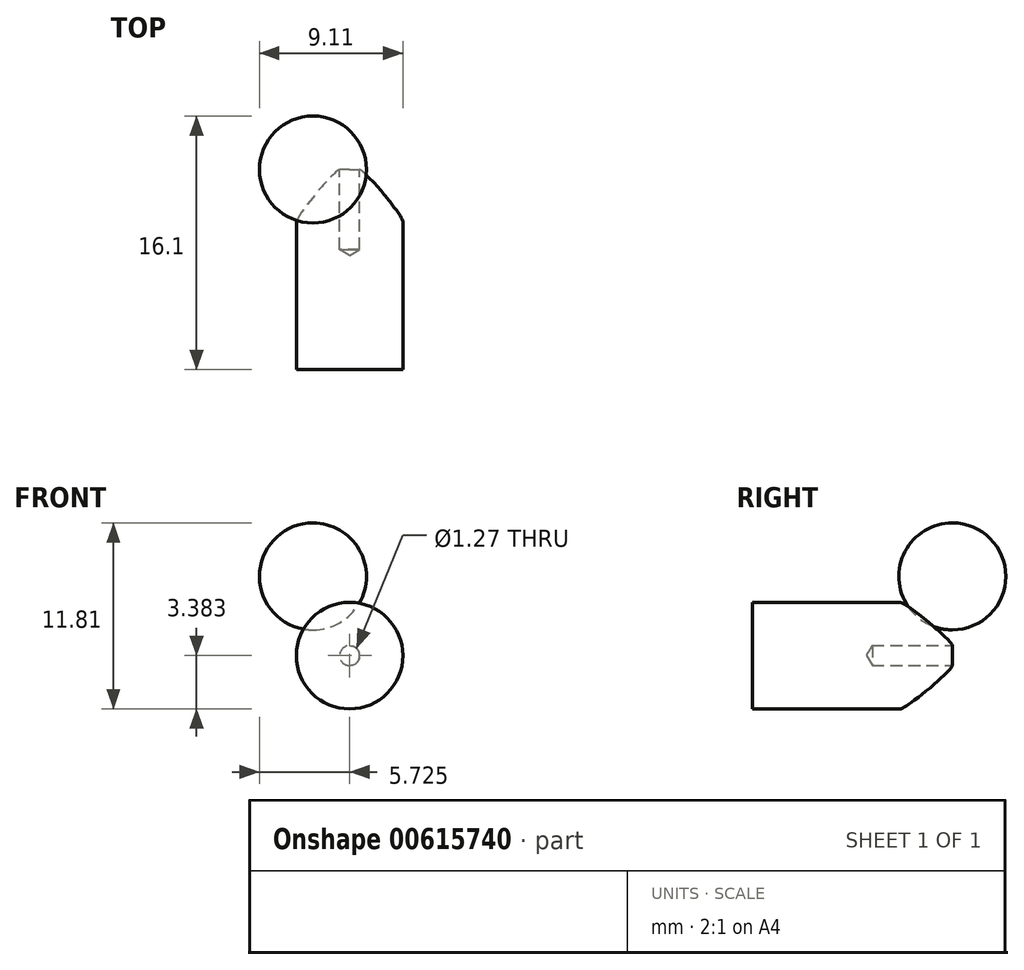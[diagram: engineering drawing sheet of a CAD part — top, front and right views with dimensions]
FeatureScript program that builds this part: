
annotation { "Feature Type Name" : "Feature", "Feature Type Description" : "" }
export const myFeature = defineFeature(function(context is Context, id is Id, definition is map)
    precondition{}
    {
        {
            var Q0;
            Q0=qCreatedBy(makeId("Front.planeOp"),FACE);
            var sketch = newSketch(context, id + "F0", { "sketchPlane" : qUnion([Q0])});
            skCircle(sketch, "E0", {"center": v(-128.5, 34.84) * mm, "radius": 3.38 * mm});
            skSolve(sketch);
        }
        {
            var Q0;
            Q0=makeQuery(id+"F0.imprint","IMPRINT",FACE,{"disambiguationData":[TD([[makeQuery(id+"F0.imprint","IMPRINT",EDGE,{"derivedFrom":sQuery(id+"F0.wireOp",EDGE,"E0")}),1.0]])]});
            extrude(context, id + "F1", {"entities" : qUnion([Q0]), "depth" : 12.7 * mm, "offsetDistance" : 25.4 * mm});
        }
        {
            var Q0;
            Q0=makeQuery(id+"F1.opExtrude","CAP_FACE",FACE,{"disambiguationData":[OSD([sQuery(id+"F0.wireOp",EDGE,"E0")])],"isStart":true});
            var sketch = newSketch(context, id + "F2", { "sketchPlane" : qUnion([Q0])});
            skCircle(sketch, "E1", {"center": v(128.5, 34.84) * mm, "radius": 5.92 * mm});
            skSolve(sketch);
        }
        {
            var Q0;
            Q0=sQuery(id+"F2.wireOp",VERTEX,"E1.center");
            var Q1;
            Q1=makeQuery(id+"F1.opExtrude","SWEPT_BODY",BODY,{"disambiguationData":[OSD([sQuery(id+"F0.wireOp",EDGE,"E0")])]});
            hole(context, id + "F3", {"style" : HoleStyle.SIMPLE, "endStyle" : HoleEndStyle.BLIND, "holeDiameter" : 1.27 * mm, "majorDiameter" : 6.35 * mm, "holeDepth" : 5.08 * mm, "isTappedThrough" : true, "tappedDepth" : 12.7 * mm, "tapClearance" : 3, "locations" : qUnion([Q0]), "scope" : qUnion([Q1])});
        }
        {
            var Q0;
            Q0=makeQuery(id+"F1.opExtrude","CAP_EDGE",EDGE,{"disambiguationData":[OSD([sQuery(id+"F0.wireOp",EDGE,"E0")])],"isStart":true});
            fillet(context, id + "F4", {"entities" : qUnion([Q0]), "radius" : 3.35 * mm, "tangentPropagation" : true, "rho" : .1, "crossSection" : FilletCrossSection.CONIC, "allowEdgeOverflow" : false});
        }
        {
            var Q0;
            Q0=qCreatedBy(makeId("Front.planeOp"),FACE);
            var sketch = newSketch(context, id + "F5", { "sketchPlane" : qUnion([Q0])});
            skCircle(sketch, "E2", {"center": v(-130.82, 39.88) * mm, "radius": 3.4 * mm});
            skLineSegment(sketch, "E3", {"start": v(-130.82, 36.48) * mm, "end": v(-130.82, 43.27) * mm});
            skSolve(sketch);
        }
        {
            var Q0;
            {var subQ0=sQuery(id+"F5.wireOp",EDGE,"E3");Q0=makeQuery(id+"F5.imprint","IMPRINT",FACE,{"disambiguationData":[TD([[makeQuery(id+"F5.imprint","IMPRINT",EDGE,{"derivedFrom":subQ0}),-1.0]])]});}
            var Q1;
            Q1=sQuery(id+"F5.wireOp",EDGE,"E3");
            revolve(context, id + "F6", {"entities" : qUnion([Q0]), "axis" : qUnion([Q1]), "revolveType" : RevolveType.FULL});
        }
    });
